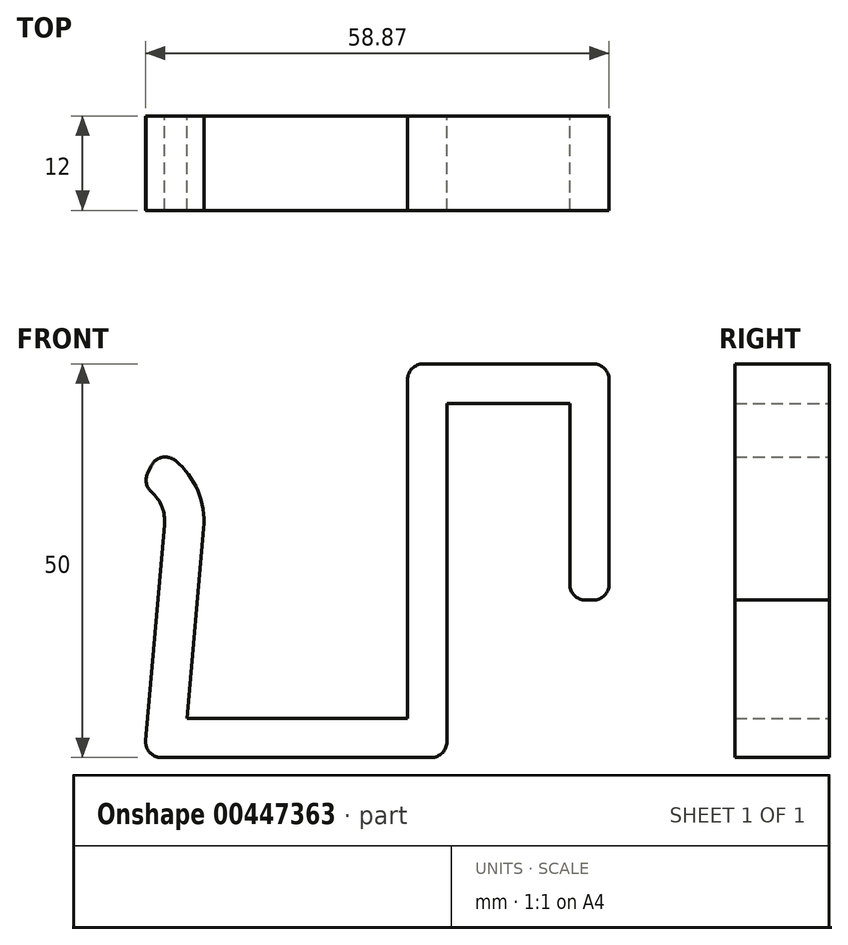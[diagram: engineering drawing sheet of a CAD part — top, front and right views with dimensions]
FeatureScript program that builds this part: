
annotation { "Feature Type Name" : "Feature", "Feature Type Description" : "" }
export const myFeature = defineFeature(function(context is Context, id is Id, definition is map)
    precondition{}
    {
        {
            var Q0;
            Q0=qCreatedBy(makeId("Front.planeOp"),FACE);
            var sketch = newSketch(context, id + "F0", { "sketchPlane" : qUnion([Q0])});
            skLineSegment(sketch, "E0", {"start": v(0, 0) * mm, "end": v(0, 25) * mm});
            skLineSegment(sketch, "E1", {"start": v(0, 25) * mm, "end": v(-15.6, 25) * mm});
            skLineSegment(sketch, "E2", {"start": v(-15.6, 25) * mm, "end": v(-15.6, -20) * mm});
            skLineSegment(sketch, "E3", {"start": v(-15.6, -20) * mm, "end": v(-54.06, -20) * mm});
            skLineSegment(sketch, "E4", {"start": v(-54.06, -20) * mm, "end": v(-51.47, 9.56) * mm});
            skArc(sketch, "E5", {"start": v(-51.47, 9.56) * mm, "mid": v(-52.12, 12.5) * mm, "end": v(-54.34, 14.53) * mm});
            skArc(sketch, "E6.0", {"start": v(-46.49, 9.13) * mm, "mid": v(-47.8, 15) * mm, "end": v(-52.22, 19.06) * mm});
            skLineSegment(sketch, "E6.1", {"start": v(-48.6, -15) * mm, "end": v(-46.49, 9.13) * mm});
            skLineSegment(sketch, "E6.2", {"start": v(5, 0) * mm, "end": v(5, 30) * mm});
            skLineSegment(sketch, "E6.3", {"start": v(5, 30) * mm, "end": v(-20.6, 30) * mm});
            skLineSegment(sketch, "E6.4", {"start": v(-20.6, 30) * mm, "end": v(-20.6, -15) * mm});
            skLineSegment(sketch, "E6.5", {"start": v(-20.6, -15) * mm, "end": v(-48.6, -15) * mm});
            skLineSegment(sketch, "E7", {"start": v(0, 0) * mm, "end": v(5, 0) * mm});
            skLineSegment(sketch, "E8", {"start": v(-56.45, 10) * mm, "end": v(-56.45, 24.3) * mm, "construction": true});
            skLineSegment(sketch, "E9", {"start": v(-54.34, 14.53) * mm, "end": v(-52.22, 19.06) * mm});
            skSolve(sketch);
        }
        {
            var Q0;
            Q0=makeQuery(id+"F0.imprint","IMPRINT",FACE,{"disambiguationData":[TD([[makeQuery(id+"F0.imprint","IMPRINT",EDGE,{"derivedFrom":sQuery(id+"F0.wireOp",EDGE,"E0")}),-1.0]])]});
            extrude(context, id + "F1", {"entities" : qUnion([Q0]), "depth" : (12) * mm});
        }
        {
            var Q0;
            Q0=makeQuery(id+"F1.opExtrude","SWEPT_EDGE",EDGE,{"disambiguationData":[OSD([sQuery(id+"F0.wireOp",EDGE,"E6.0"),sQuery(id+"F0.wireOp",EDGE,"E9")])]});
            var Q1;
            Q1=makeQuery(id+"F1.opExtrude","SWEPT_EDGE",EDGE,{"disambiguationData":[OSD([sQuery(id+"F0.wireOp",EDGE,"E5"),sQuery(id+"F0.wireOp",EDGE,"E9")])]});
            var Q2;
            Q2=makeQuery(id+"F1.opExtrude","SWEPT_EDGE",EDGE,{"disambiguationData":[OSD([sQuery(id+"F0.wireOp",EDGE,"E3"),sQuery(id+"F0.wireOp",EDGE,"E4")])]});
            var Q3;
            Q3=makeQuery(id+"F1.opExtrude","SWEPT_EDGE",EDGE,{"disambiguationData":[OSD([sQuery(id+"F0.wireOp",EDGE,"E2"),sQuery(id+"F0.wireOp",EDGE,"E3")])]});
            var Q4;
            Q4=makeQuery(id+"F1.opExtrude","SWEPT_EDGE",EDGE,{"disambiguationData":[OSD([sQuery(id+"F0.wireOp",EDGE,"E6.2"),sQuery(id+"F0.wireOp",EDGE,"E6.3")])]});
            var Q5;
            Q5=makeQuery(id+"F1.opExtrude","SWEPT_EDGE",EDGE,{"disambiguationData":[OSD([sQuery(id+"F0.wireOp",EDGE,"E6.3"),sQuery(id+"F0.wireOp",EDGE,"E6.4")])]});
            var Q6;
            Q6=makeQuery(id+"F1.opExtrude","SWEPT_EDGE",EDGE,{"disambiguationData":[OSD([sQuery(id+"F0.wireOp",EDGE,"E0"),sQuery(id+"F0.wireOp",EDGE,"E7")])]});
            var Q7;
            Q7=makeQuery(id+"F1.opExtrude","SWEPT_EDGE",EDGE,{"disambiguationData":[OSD([sQuery(id+"F0.wireOp",EDGE,"E6.2"),sQuery(id+"F0.wireOp",EDGE,"E7")])]});
            fillet(context, id + "F2", {"entities" : qUnion([Q0, Q1, Q2, Q3, Q4, Q5, Q6, Q7]), "radius" : (2) * mm, "tangentPropagation" : true, "allowEdgeOverflow" : false});
        }
    });
